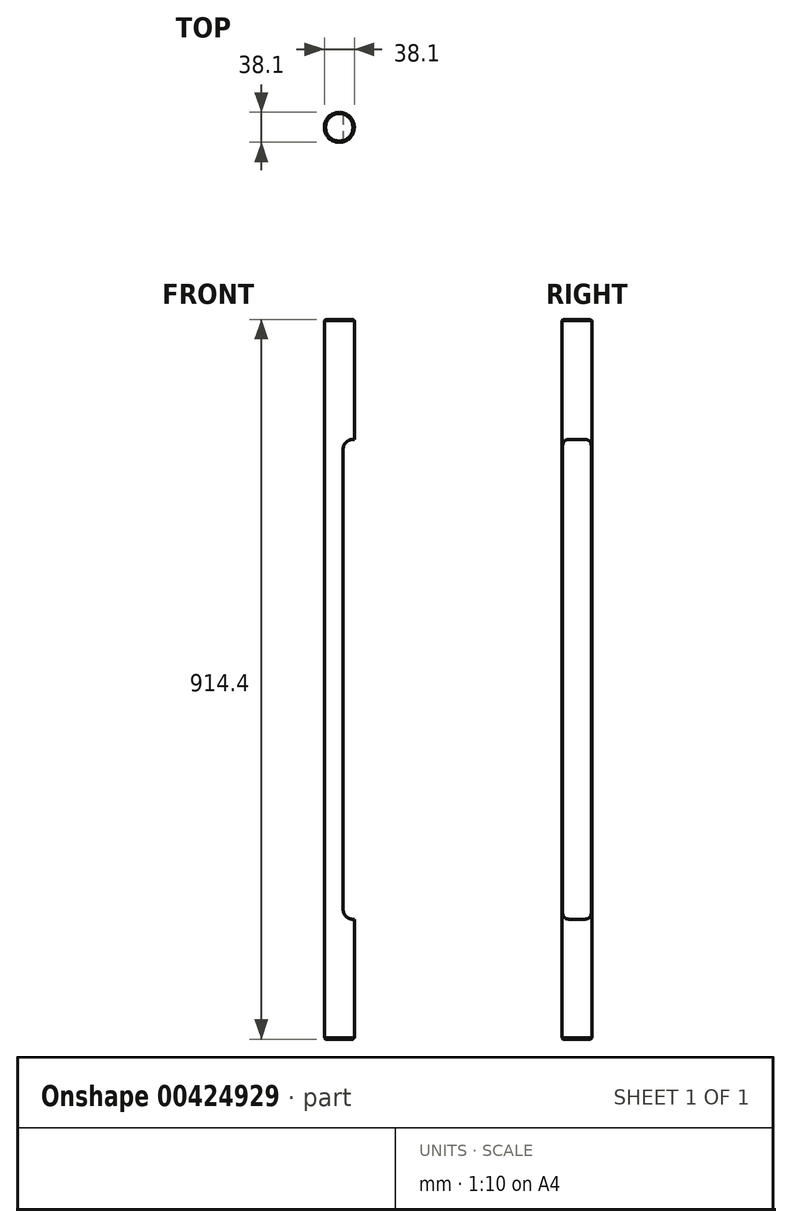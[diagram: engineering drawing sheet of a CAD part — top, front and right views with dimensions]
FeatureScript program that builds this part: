
annotation { "Feature Type Name" : "Feature", "Feature Type Description" : "" }
export const myFeature = defineFeature(function(context is Context, id is Id, definition is map)
    precondition{}
    {
        {
            var Q0;
            Q0=qCreatedBy(makeId("Top.planeOp"),FACE);
            var sketch = newSketch(context, id + "F0", { "sketchPlane" : qUnion([Q0])});
            skCircle(sketch, "E0", {"center": v(0, 0) * mm, "radius": 19.05 * mm});
            skSolve(sketch);
        }
        {
            var Q0;
            Q0=makeQuery(id+"F0.imprint","IMPRINT",FACE,{"disambiguationData":[TD([[makeQuery(id+"F0.imprint","IMPRINT",EDGE,{"derivedFrom":sQuery(id+"F0.wireOp",EDGE,"E0")}),1.0]])]});
            extrude(context, id + "F1", {"entities" : qUnion([Q0]), "depth" : 914.4 * mm, "symmetric" : true});
        }
        {
            var Q0;
            Q0=makeQuery(id+"F1.opExtrude","CAP_EDGE",EDGE,{"disambiguationData":[OSD([sQuery(id+"F0.wireOp",EDGE,"E0")])],"isStart":false});
            var Q1;
            Q1=makeQuery(id+"F1.opExtrude","CAP_EDGE",EDGE,{"disambiguationData":[OSD([sQuery(id+"F0.wireOp",EDGE,"E0")])],"isStart":true});
            chamfer(context, id + "F2", {"entities" : qUnion([Q0, Q1]), "chamferType" : ChamferType.OFFSET_ANGLE, "width" : 1.59 * mm, "oppositeDirection" : false, "angle" : 45 * degree, "tangentPropagation" : true});
        }
        {
            var Q0;
            Q0=qCreatedBy(makeId("Front.planeOp"),FACE);
            var sketch = newSketch(context, id + "F3", { "sketchPlane" : qUnion([Q0])});
            skLineSegment(sketch, "E1", {"start": v(0, -317.38) * mm, "end": v(0, 362.95) * mm, "construction": true});
            skLineSegment(sketch, "E2", {"start": v(4.78, -292.1) * mm, "end": v(4.78, 304.8) * mm});
            skLineSegment(sketch, "E3", {"start": v(-36.1, 0) * mm, "end": v(39.14, 0) * mm, "construction": true});
            skArc(sketch, "E4", {"start": v(4.78, -292.1) * mm, "mid": v(17.48, -304.8) * mm, "end": v(30.18, -292.1) * mm});
            skPoint(sketch, "E5.orphan", {"position": v(4.78, -304.8) * mm});
            skArc(sketch, "E6.MirrorC", {"start": v(4.78, 292.1) * mm, "mid": v(17.48, 304.8) * mm, "end": v(30.18, 292.1) * mm});
            skLineSegment(sketch, "E7", {"start": v(30.18, -292.1) * mm, "end": v(30.18, 292.1) * mm});
            skSolve(sketch);
        }
        {
            var Q0;
            {var subQ0=sQuery(id+"F3.wireOp",EDGE,"E4");Q0=makeQuery(id+"F3.imprint","IMPRINT",FACE,{"disambiguationData":[TD([[makeQuery(id+"F3.imprint","IMPRINT",EDGE,{"derivedFrom":subQ0}),1.0]])]});}
            extrude(context, id + "F4", {"entities" : qUnion([Q0]), "operationType" : NewBodyOperationType.REMOVE, "oppositeDirection" : true, "depth" : 38.1 * mm, "symmetric" : true});
        }
    });
